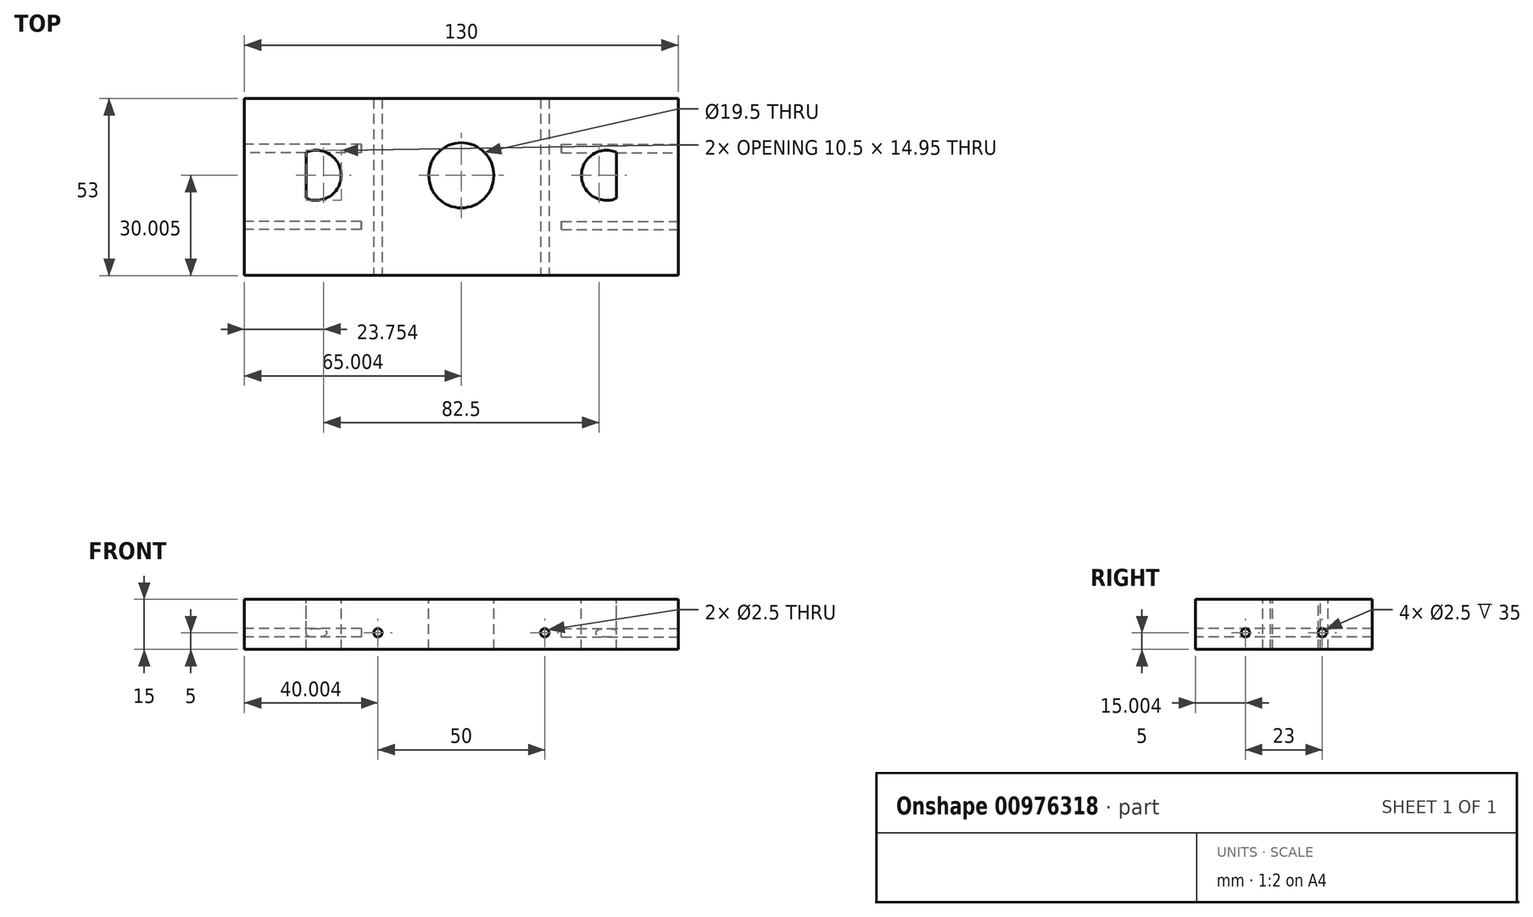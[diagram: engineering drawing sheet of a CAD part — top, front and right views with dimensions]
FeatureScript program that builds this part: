
annotation { "Feature Type Name" : "Feature", "Feature Type Description" : "" }
export const myFeature = defineFeature(function(context is Context, id is Id, definition is map)
    precondition{}
    {
        {
            var Q0;
            Q0=qCreatedBy(makeId("Top.planeOp"),FACE);
            var sketch = newSketch(context, id + "F0", { "sketchPlane" : qUnion([Q0])});
            skLineSegment(sketch, "E0.bottom", {"start": v(-44.98, 28.62) * mm, "end": v(85.02, 28.62) * mm});
            skLineSegment(sketch, "E0.top", {"start": v(-44.98, -24.38) * mm, "end": v(85.02, -24.38) * mm});
            skLineSegment(sketch, "E0.left", {"start": v(-44.98, 28.62) * mm, "end": v(-44.98, -24.38) * mm});
            skLineSegment(sketch, "E0.right", {"start": v(85.02, 28.62) * mm, "end": v(85.02, -24.38) * mm});
            skSolve(sketch);
        }
        {
            var Q0;
            Q0=makeQuery(id+"F0.imprint","IMPRINT",FACE,{"disambiguationData":[TD([[makeQuery(id+"F0.imprint","IMPRINT",EDGE,{"derivedFrom":sQuery(id+"F0.wireOp",EDGE,"E0.bottom")}),-1.0]])]});
            extrude(context, id + "F1", {"entities" : qUnion([Q0]), "depth" : 15 * mm, "offsetDistance" : 25 * mm});
        }
        {
            var Q0;
            Q0=makeQuery(id+"F1.opExtrude","SWEPT_FACE",FACE,{"disambiguationData":[OSD([sQuery(id+"F0.wireOp",EDGE,"E0.right")])]});
            var sketch = newSketch(context, id + "F2", { "sketchPlane" : qUnion([Q0])});
            skCircle(sketch, "E1", {"center": v(-9.38, 5) * mm, "radius": 1.25 * mm});
            skCircle(sketch, "E2", {"center": v(13.62, 5) * mm, "radius": 1.25 * mm});
            skSolve(sketch);
        }
        {
            var Q0;
            Q0=makeQuery(id+"F1.opExtrude","SWEPT_FACE",FACE,{"disambiguationData":[OSD([sQuery(id+"F0.wireOp",EDGE,"E0.top")])]});
            var sketch = newSketch(context, id + "F3", { "sketchPlane" : qUnion([Q0])});
            skCircle(sketch, "E3", {"center": v(-4.98, 5) * mm, "radius": 1.25 * mm});
            skCircle(sketch, "E4", {"center": v(45.02, 5) * mm, "radius": 1.25 * mm});
            skSolve(sketch);
        }
        {
            var Q0;
            Q0=makeQuery(id+"F1.opExtrude","SWEPT_FACE",FACE,{"disambiguationData":[OSD([sQuery(id+"F0.wireOp",EDGE,"E0.left")])]});
            var sketch = newSketch(context, id + "F4", { "sketchPlane" : qUnion([Q0])});
            skCircle(sketch, "E5", {"center": v(-13.62, 5) * mm, "radius": 1.25 * mm});
            skCircle(sketch, "E6", {"center": v(9.38, 5) * mm, "radius": 1.25 * mm});
            skSolve(sketch);
        }
        {
            var Q0;
            Q0=qSketchRegion(id+"F2",true);
            extrude(context, id + "F5", {"entities" : qUnion([Q0]), "operationType" : NewBodyOperationType.REMOVE, "oppositeDirection" : true, "depth" : 35 * mm, "offsetDistance" : 25 * mm});
        }
        {
            var Q0;
            Q0=qSketchRegion(id+"F3",true);
            extrude(context, id + "F6", {"entities" : qUnion([Q0]), "operationType" : NewBodyOperationType.REMOVE, "endBound" : BoundingType.UP_TO_NEXT, "oppositeDirection" : true, "depth" : 25 * mm, "offsetDistance" : 25 * mm});
        }
        {
            var Q0;
            Q0=qSketchRegion(id+"F4",true);
            extrude(context, id + "F7", {"entities" : qUnion([Q0]), "operationType" : NewBodyOperationType.REMOVE, "oppositeDirection" : true, "depth" : 35 * mm, "offsetDistance" : 25 * mm});
        }
        {
            var Q0;
            Q0=makeQuery(id+"F1.opExtrude","CAP_FACE",FACE,{"disambiguationData":[OSD([sQuery(id+"F0.wireOp",EDGE,"E0.bottom"),sQuery(id+"F0.wireOp",EDGE,"E0.top"),sQuery(id+"F0.wireOp",EDGE,"E0.left"),sQuery(id+"F0.wireOp",EDGE,"E0.right")])],"isStart":false});
            var sketch = newSketch(context, id + "F8", { "sketchPlane" : qUnion([Q0])});
            skCircle(sketch, "E7", {"center": v(-23.48, 5.62) * mm, "radius": 7.5 * mm});
            skCircle(sketch, "E8", {"center": v(63.52, 5.62) * mm, "radius": 7.5 * mm});
            skLineSegment(sketch, "E9", {"start": v(-26.48, 12.5) * mm, "end": v(-26.48, -1.25) * mm});
            skLineSegment(sketch, "E10", {"start": v(66.52, 12.5) * mm, "end": v(66.52, -1.25) * mm});
            skSolve(sketch);
        }
        {
            var Q0;
            {var subQ0=sQuery(id+"F8.wireOp",EDGE,"E10");Q0=makeQuery(id+"F8.imprint","IMPRINT",FACE,{"disambiguationData":[TD([[makeQuery(id+"F8.imprint","IMPRINT",EDGE,{"derivedFrom":subQ0}),-1.0]])]});}
            var Q1;
            {var subQ0=sQuery(id+"F8.wireOp",EDGE,"E9");Q1=makeQuery(id+"F8.imprint","IMPRINT",FACE,{"disambiguationData":[TD([[makeQuery(id+"F8.imprint","IMPRINT",EDGE,{"derivedFrom":subQ0}),1.0]])]});}
            extrude(context, id + "F9", {"entities" : qUnion([Q0, Q1]), "operationType" : NewBodyOperationType.REMOVE, "endBound" : BoundingType.UP_TO_NEXT, "oppositeDirection" : true, "depth" : 25 * mm, "offsetDistance" : 25 * mm});
        }
        {
            var Q0;
            Q0=makeQuery(id+"F1.opExtrude","CAP_FACE",FACE,{"disambiguationData":[OSD([sQuery(id+"F0.wireOp",EDGE,"E0.bottom"),sQuery(id+"F0.wireOp",EDGE,"E0.top"),sQuery(id+"F0.wireOp",EDGE,"E0.left"),sQuery(id+"F0.wireOp",EDGE,"E0.right")])],"isStart":false});
            var sketch = newSketch(context, id + "F10", { "sketchPlane" : qUnion([Q0])});
            skCircle(sketch, "E11", {"center": v(20.02, 5.62) * mm, "radius": 9.75 * mm});
            skSolve(sketch);
        }
        {
            var Q0;
            Q0=makeQuery(id+"F10.imprint","IMPRINT",FACE,{"disambiguationData":[TD([[makeQuery(id+"F10.imprint","IMPRINT",EDGE,{"derivedFrom":sQuery(id+"F10.wireOp",EDGE,"E11")}),1.0]])]});
            extrude(context, id + "F11", {"entities" : qUnion([Q0]), "operationType" : NewBodyOperationType.REMOVE, "endBound" : BoundingType.UP_TO_NEXT, "oppositeDirection" : true, "depth" : 25 * mm, "offsetDistance" : 25 * mm});
        }
    });
